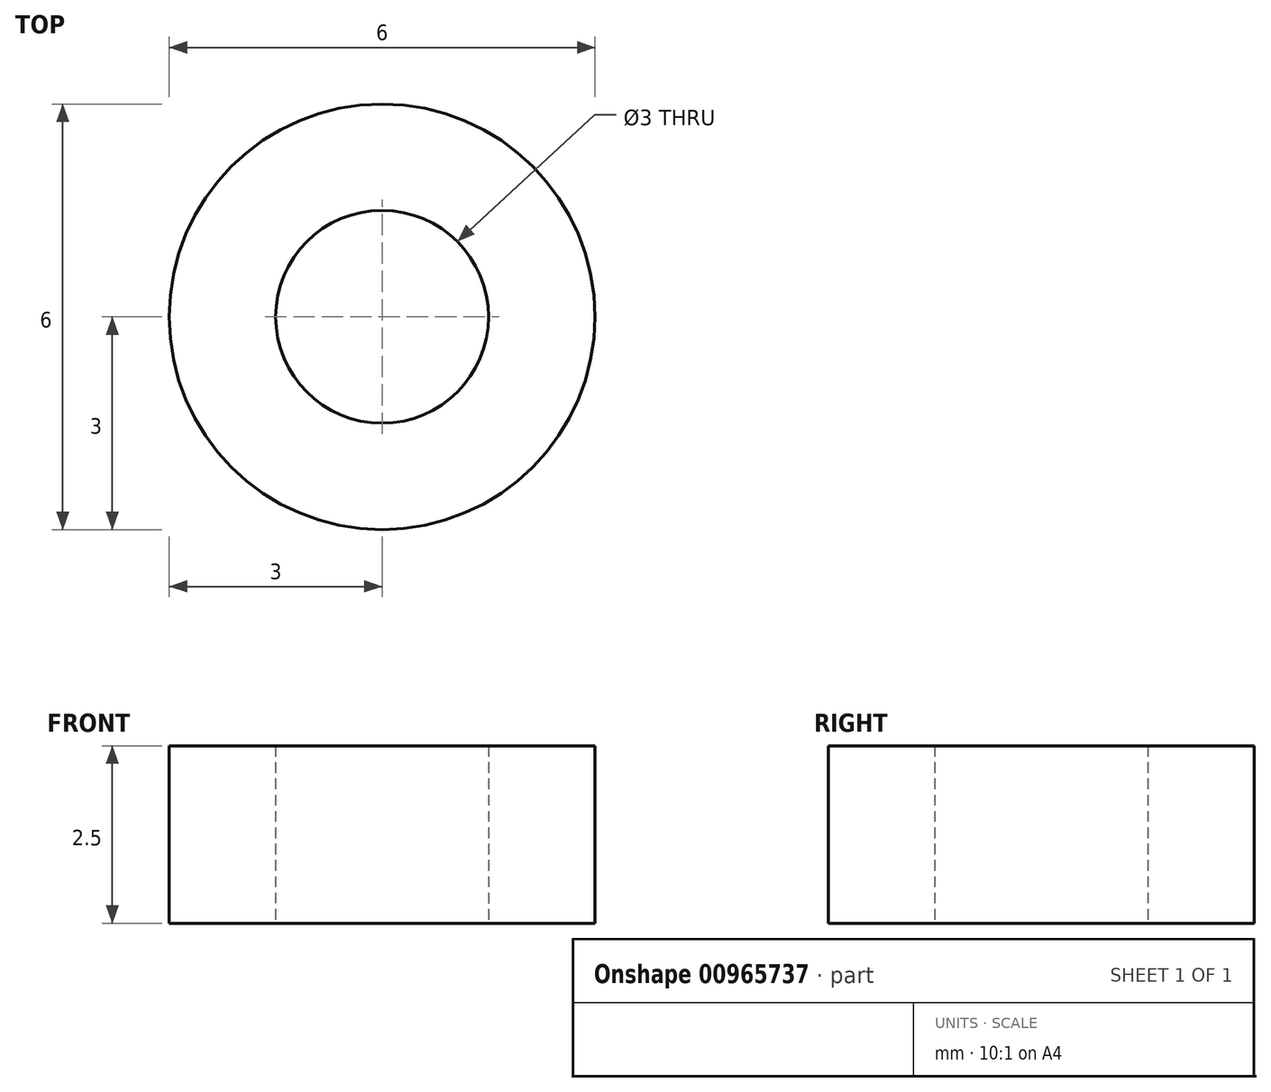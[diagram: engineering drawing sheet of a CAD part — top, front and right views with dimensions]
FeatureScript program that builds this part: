
annotation { "Feature Type Name" : "Feature", "Feature Type Description" : "" }
export const myFeature = defineFeature(function(context is Context, id is Id, definition is map)
    precondition{}
    {
        {
            var Q0;
            Q0=qCreatedBy(makeId("Top.planeOp"),FACE);
            var sketch = newSketch(context, id + "F0", { "sketchPlane" : qUnion([Q0])});
            skCircle(sketch, "E0", {"center": v(0, 0) * mm, "radius": 3 * mm});
            skCircle(sketch, "E1", {"center": v(0, 0) * mm, "radius": 1.5 * mm});
            skSolve(sketch);
        }
        {
            var Q0;
            Q0 = qSketchRegion(id + "F0", true);
            extrude(context, id + "F1", {"entities" : qUnion([Q0]), "depth" : 2.5 * mm, "offsetDistance" : 25 * mm});
        }
    });
